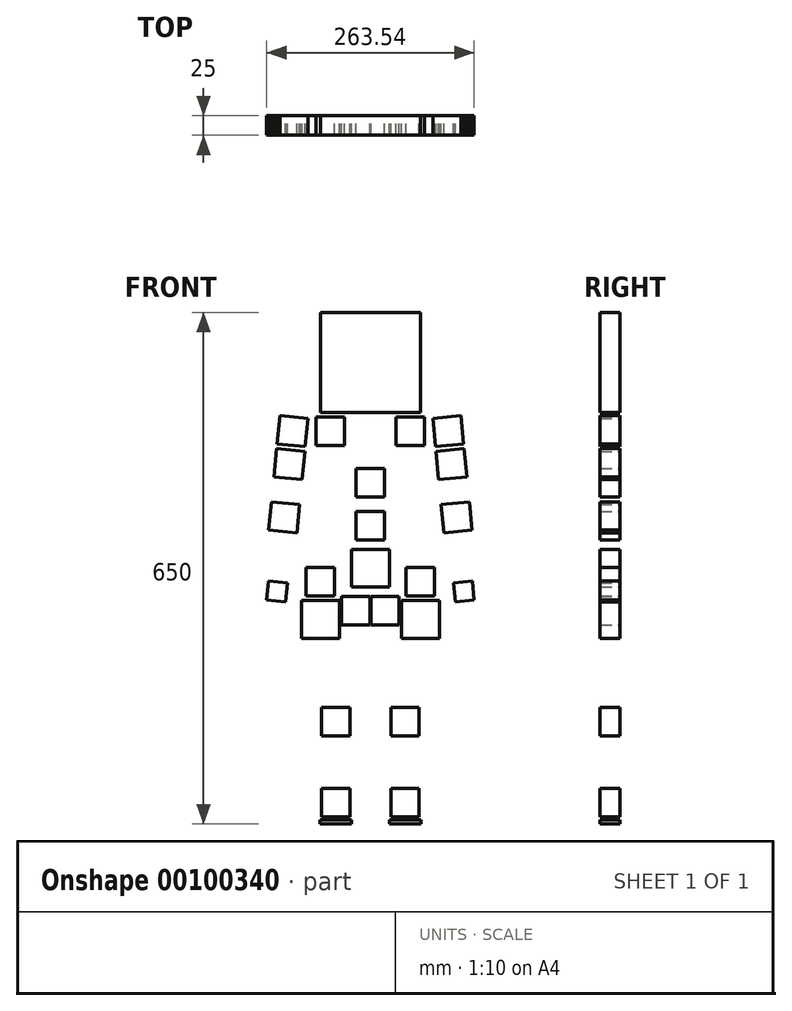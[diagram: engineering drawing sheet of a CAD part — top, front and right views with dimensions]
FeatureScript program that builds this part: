
annotation { "Feature Type Name" : "Feature", "Feature Type Description" : "" }
export const myFeature = defineFeature(function(context is Context, id is Id, definition is map)
    precondition{}
    {
        {
            var Q0;
            Q0=qCreatedBy(makeId("Front.planeOp"),FACE);
            var sketch = newSketch(context, id + "F0", { "sketchPlane" : qUnion([Q0])});
            skLineSegment(sketch, "E0.bottom", {"start": v(-190.27, 650) * mm, "end": v(190.27, 650) * mm, "construction": true});
            skLineSegment(sketch, "E0.top", {"start": v(-190.27, 0) * mm, "end": v(190.27, 0) * mm, "construction": true});
            skLineSegment(sketch, "E1", {"start": v(0, 0) * mm, "end": v(0, 650) * mm, "construction": true});
            skLineSegment(sketch, "E2", {"start": v(-190.27, 520) * mm, "end": v(190.27, 520) * mm, "construction": true});
            skLineSegment(sketch, "E3", {"start": v(-190.27, 650) * mm, "end": v(-190.27, 520) * mm, "construction": true});
            skLineSegment(sketch, "E4", {"start": v(-190.27, 0) * mm, "end": v(-190.27, 520) * mm, "construction": true});
            skLineSegment(sketch, "E5", {"start": v(-190.27, 260) * mm, "end": v(190.27, 260) * mm, "construction": true});
            skLineSegment(sketch, "E6", {"start": v(-81.25, 260) * mm, "end": v(-81.25, 0) * mm, "construction": true});
            skLineSegment(sketch, "E7", {"start": v(81.25, 260) * mm, "end": v(81.25, 0) * mm, "construction": true});
            skLineSegment(sketch, "E8", {"start": v(-81.25, 130) * mm, "end": v(81.25, 130) * mm, "construction": true});
            skLineSegment(sketch, "E9", {"start": v(190.27, 650) * mm, "end": v(190.27, 0) * mm, "construction": true});
            skLineSegment(sketch, "E10", {"start": v(190.27, 325) * mm, "end": v(-190.27, 325) * mm, "construction": true});
            skSolve(sketch);
        }
        {
            var Q0;
            Q0=qCreatedBy(makeId("Front.planeOp"),FACE);
            var sketch = newSketch(context, id + "F1", { "sketchPlane" : qUnion([Q0])});
            skLineSegment(sketch, "E11", {"start": v(0, 260) * mm, "end": v(63.5, 260) * mm, "construction": true});
            skLineSegment(sketch, "E12", {"start": v(63.5, 260) * mm, "end": v(44, 130) * mm, "construction": true});
            skLineSegment(sketch, "E13", {"start": v(44, 130) * mm, "end": v(44, 27.18) * mm, "construction": true});
            skLineSegment(sketch, "E14", {"start": v(44, 27.18) * mm, "end": v(44, 0) * mm, "construction": true});
            skLineSegment(sketch, "E15", {"start": v(0, 0) * mm, "end": v(0, 650) * mm, "construction": true});
            skLineSegment(sketch, "E16.bottom", {"start": v(62, 9.18) * mm, "end": v(26, 9.18) * mm});
            skLineSegment(sketch, "E16.top", {"start": v(62, 45.18) * mm, "end": v(26, 45.18) * mm});
            skLineSegment(sketch, "E16.left", {"start": v(62, 9.18) * mm, "end": v(62, 45.18) * mm});
            skLineSegment(sketch, "E16.right", {"start": v(26, 9.18) * mm, "end": v(26, 45.18) * mm});
            skPoint(sketch, "E16.middle", {"position": v(44, 27.18) * mm});
            skLineSegment(sketch, "E17.bottom", {"start": v(62, 112) * mm, "end": v(26, 112) * mm});
            skLineSegment(sketch, "E17.top", {"start": v(62, 148) * mm, "end": v(26, 148) * mm});
            skLineSegment(sketch, "E17.left", {"start": v(62, 112) * mm, "end": v(62, 148) * mm});
            skLineSegment(sketch, "E17.right", {"start": v(26, 112) * mm, "end": v(26, 148) * mm});
            skPoint(sketch, "E17.middle", {"position": v(44, 130) * mm});
            skLineSegment(sketch, "E18.bottom", {"start": v(87.5, 236) * mm, "end": v(39.5, 236) * mm});
            skLineSegment(sketch, "E18.top", {"start": v(87.5, 284) * mm, "end": v(39.5, 284) * mm});
            skLineSegment(sketch, "E18.left", {"start": v(87.5, 236) * mm, "end": v(87.5, 284) * mm});
            skLineSegment(sketch, "E18.right", {"start": v(39.5, 236) * mm, "end": v(39.5, 284) * mm});
            skPoint(sketch, "E18.middle", {"position": v(63.5, 260) * mm});
            skLineSegment(sketch, "E19.bottom", {"start": v(81.5, 290) * mm, "end": v(45.5, 290) * mm});
            skLineSegment(sketch, "E19.top", {"start": v(81.5, 326) * mm, "end": v(45.5, 326) * mm});
            skLineSegment(sketch, "E19.left", {"start": v(81.5, 290) * mm, "end": v(81.5, 326) * mm});
            skLineSegment(sketch, "E19.right", {"start": v(45.5, 290) * mm, "end": v(45.5, 326) * mm});
            skPoint(sketch, "E19.middle", {"position": v(63.5, 308) * mm});
            skLineSegment(sketch, "E20.bottom", {"start": v(36.5, 253) * mm, "end": v(0.5, 253) * mm});
            skLineSegment(sketch, "E20.top", {"start": v(36.5, 289) * mm, "end": v(0.5, 289) * mm});
            skLineSegment(sketch, "E20.left", {"start": v(36.5, 253) * mm, "end": v(36.5, 289) * mm});
            skLineSegment(sketch, "E20.right", {"start": v(0.5, 253) * mm, "end": v(0.5, 289) * mm});
            skPoint(sketch, "E20.middle", {"position": v(18.5, 271) * mm});
            skLineSegment(sketch, "E21.bottom", {"start": v(24, 301) * mm, "end": v(-24, 301) * mm});
            skLineSegment(sketch, "E21.top", {"start": v(24, 349) * mm, "end": v(-24, 349) * mm});
            skLineSegment(sketch, "E21.left", {"start": v(24, 301) * mm, "end": v(24, 349) * mm});
            skLineSegment(sketch, "E21.right", {"start": v(-24, 301) * mm, "end": v(-24, 349) * mm});
            skPoint(sketch, "E21.middle", {"position": v(0, 325) * mm});
            skLineSegment(sketch, "E22.bottom", {"start": v(18, 361) * mm, "end": v(-18, 361) * mm});
            skLineSegment(sketch, "E22.top", {"start": v(18, 397) * mm, "end": v(-18, 397) * mm});
            skLineSegment(sketch, "E22.left", {"start": v(18, 361) * mm, "end": v(18, 397) * mm});
            skLineSegment(sketch, "E22.right", {"start": v(-18, 361) * mm, "end": v(-18, 397) * mm});
            skPoint(sketch, "E22.middle", {"position": v(0, 379) * mm});
            skLineSegment(sketch, "E23.bottom", {"start": v(18, 415.45) * mm, "end": v(-18, 415.45) * mm});
            skLineSegment(sketch, "E23.top", {"start": v(18, 451.45) * mm, "end": v(-18, 451.45) * mm});
            skLineSegment(sketch, "E23.left", {"start": v(18, 415.45) * mm, "end": v(18, 451.45) * mm});
            skLineSegment(sketch, "E23.right", {"start": v(-18, 415.45) * mm, "end": v(-18, 451.45) * mm});
            skPoint(sketch, "E23.middle", {"position": v(0, 433.45) * mm});
            skLineSegment(sketch, "E24.MirrorCS", {"start": v(-26, 9.18) * mm, "end": v(-26, 45.18) * mm});
            skLineSegment(sketch, "E25.MirrorCS", {"start": v(-45.5, 290) * mm, "end": v(-45.5, 326) * mm});
            skLineSegment(sketch, "E26.MirrorCS", {"start": v(-81.5, 290) * mm, "end": v(-81.5, 326) * mm});
            skPoint(sketch, "E27.MirrorP", {"position": v(-44, 27.18) * mm});
            skLineSegment(sketch, "E28.MirrorCS", {"start": v(-87.5, 236) * mm, "end": v(-39.5, 236) * mm});
            skLineSegment(sketch, "E29.MirrorCS", {"start": v(-87.5, 284) * mm, "end": v(-39.5, 284) * mm});
            skLineSegment(sketch, "E30.MirrorCS", {"start": v(-81.5, 326) * mm, "end": v(-45.5, 326) * mm});
            skLineSegment(sketch, "E31.MirrorCS", {"start": v(-36.5, 289) * mm, "end": v(-0.5, 289) * mm});
            skLineSegment(sketch, "E32.MirrorCS", {"start": v(-62, 9.18) * mm, "end": v(-62, 45.18) * mm});
            skLineSegment(sketch, "E33.MirrorCS", {"start": v(-62, 45.18) * mm, "end": v(-26, 45.18) * mm});
            skLineSegment(sketch, "E34.MirrorCS", {"start": v(-62, 112) * mm, "end": v(-26, 112) * mm});
            skLineSegment(sketch, "E35.MirrorCS", {"start": v(-87.5, 236) * mm, "end": v(-87.5, 284) * mm});
            skLineSegment(sketch, "E36.MirrorCS", {"start": v(-62, 148) * mm, "end": v(-26, 148) * mm});
            skLineSegment(sketch, "E37.MirrorCS", {"start": v(0, 260) * mm, "end": v(-63.5, 260) * mm, "construction": true});
            skLineSegment(sketch, "E38.MirrorCS", {"start": v(-62, 112) * mm, "end": v(-62, 148) * mm});
            skLineSegment(sketch, "E39.MirrorCS", {"start": v(-62, 9.18) * mm, "end": v(-26, 9.18) * mm});
            skLineSegment(sketch, "E40.MirrorCS", {"start": v(-44, 27.18) * mm, "end": v(-44, 0) * mm, "construction": true});
            skPoint(sketch, "E41.MirrorP", {"position": v(-63.5, 308) * mm});
            skLineSegment(sketch, "E42.MirrorCS", {"start": v(-81.5, 290) * mm, "end": v(-45.5, 290) * mm});
            skLineSegment(sketch, "E43.MirrorCS", {"start": v(-63.5, 260) * mm, "end": v(-44, 130) * mm, "construction": true});
            skLineSegment(sketch, "E44.MirrorCS", {"start": v(-44, 130) * mm, "end": v(-44, 27.18) * mm, "construction": true});
            skPoint(sketch, "E45.MirrorP", {"position": v(-63.5, 260) * mm});
            skPoint(sketch, "E46.MirrorP", {"position": v(-18.5, 271) * mm});
            skLineSegment(sketch, "E47.MirrorCS", {"start": v(-36.5, 253) * mm, "end": v(-36.5, 289) * mm});
            skLineSegment(sketch, "E48.MirrorCS", {"start": v(-26, 112) * mm, "end": v(-26, 148) * mm});
            skLineSegment(sketch, "E49.MirrorCS", {"start": v(-0.5, 253) * mm, "end": v(-0.5, 289) * mm});
            skPoint(sketch, "E50.MirrorP", {"position": v(-44, 130) * mm});
            skLineSegment(sketch, "E51.MirrorCS", {"start": v(-39.5, 236) * mm, "end": v(-39.5, 284) * mm});
            skLineSegment(sketch, "E52.MirrorCS", {"start": v(-36.5, 253) * mm, "end": v(-0.5, 253) * mm});
            skLineSegment(sketch, "E53", {"start": v(0, 499) * mm, "end": v(98.88, 499) * mm, "construction": true});
            skPoint(sketch, "E54.middle", {"position": v(98.88, 499) * mm});
            skLineSegment(sketch, "E55.bottom", {"start": v(68.88, 481) * mm, "end": v(32.88, 481) * mm});
            skLineSegment(sketch, "E55.top", {"start": v(68.88, 517) * mm, "end": v(32.88, 517) * mm});
            skLineSegment(sketch, "E55.left", {"start": v(68.88, 481) * mm, "end": v(68.88, 517) * mm});
            skLineSegment(sketch, "E55.right", {"start": v(32.88, 481) * mm, "end": v(32.88, 517) * mm});
            skPoint(sketch, "E55.middle", {"position": v(50.88, 499) * mm});
            skLineSegment(sketch, "E56", {"start": v(98.88, 499) * mm, "end": v(109.51, 389.55) * mm, "construction": true});
            skLineSegment(sketch, "E57", {"start": v(109.51, 389.55) * mm, "end": v(118.66, 295.4) * mm, "construction": true});
            skLineSegment(sketch, "E58", {"start": v(118.66, 295.4) * mm, "end": v(124.13, 239.15) * mm, "construction": true});
            skLineSegment(sketch, "E59.bottom", {"start": v(129.17, 373.38) * mm, "end": v(93.34, 369.9) * mm});
            skLineSegment(sketch, "E59.top", {"start": v(125.69, 409.2) * mm, "end": v(89.86, 405.73) * mm});
            skLineSegment(sketch, "E59.left", {"start": v(129.17, 373.38) * mm, "end": v(125.69, 409.2) * mm});
            skLineSegment(sketch, "E59.right", {"start": v(93.34, 369.9) * mm, "end": v(89.86, 405.73) * mm});
            skPoint(sketch, "E59.middle", {"position": v(109.51, 389.55) * mm});
            skLineSegment(sketch, "E60.bottom", {"start": v(122.6, 441.02) * mm, "end": v(86.77, 437.54) * mm});
            skLineSegment(sketch, "E60.top", {"start": v(119.12, 476.85) * mm, "end": v(83.29, 473.37) * mm});
            skLineSegment(sketch, "E60.left", {"start": v(122.6, 441.02) * mm, "end": v(119.12, 476.85) * mm});
            skLineSegment(sketch, "E60.right", {"start": v(86.77, 437.54) * mm, "end": v(83.29, 473.37) * mm});
            skPoint(sketch, "E60.middle", {"position": v(102.94, 457.2) * mm});
            skLineSegment(sketch, "E61.bottom", {"start": v(118.54, 482.83) * mm, "end": v(82.7, 479.34) * mm});
            skLineSegment(sketch, "E61.top", {"start": v(115.05, 518.66) * mm, "end": v(79.22, 515.17) * mm});
            skLineSegment(sketch, "E61.left", {"start": v(118.54, 482.83) * mm, "end": v(115.05, 518.66) * mm});
            skLineSegment(sketch, "E61.right", {"start": v(82.7, 479.34) * mm, "end": v(79.22, 515.17) * mm});
            skLineSegment(sketch, "E62.bottom", {"start": v(107.88, 282.3) * mm, "end": v(105.56, 306.19) * mm});
            skLineSegment(sketch, "E62.top", {"start": v(131.77, 284.62) * mm, "end": v(129.45, 308.51) * mm});
            skLineSegment(sketch, "E62.left", {"start": v(107.88, 282.3) * mm, "end": v(131.77, 284.62) * mm});
            skLineSegment(sketch, "E62.right", {"start": v(105.56, 306.19) * mm, "end": v(129.45, 308.51) * mm});
            skPoint(sketch, "E62.middle", {"position": v(118.66, 295.4) * mm});
            skPoint(sketch, "E63.MirrorP", {"position": v(-98.88, 499) * mm});
            skPoint(sketch, "E64.MirrorP", {"position": v(-102.94, 457.2) * mm});
            skPoint(sketch, "E65.MirrorP", {"position": v(-109.51, 389.55) * mm});
            skLineSegment(sketch, "E66.MirrorCS", {"start": v(-122.6, 441.02) * mm, "end": v(-119.12, 476.85) * mm});
            skLineSegment(sketch, "E67.MirrorCS", {"start": v(-105.56, 306.19) * mm, "end": v(-129.45, 308.51) * mm});
            skLineSegment(sketch, "E68.MirrorCS", {"start": v(-118.54, 482.83) * mm, "end": v(-82.7, 479.34) * mm});
            skLineSegment(sketch, "E69.MirrorCS", {"start": v(0, 499) * mm, "end": v(-98.88, 499) * mm, "construction": true});
            skLineSegment(sketch, "E70.MirrorCS", {"start": v(-118.66, 295.4) * mm, "end": v(-124.13, 239.15) * mm, "construction": true});
            skLineSegment(sketch, "E71.MirrorCS", {"start": v(-82.7, 479.34) * mm, "end": v(-79.22, 515.17) * mm});
            skLineSegment(sketch, "E72.MirrorCS", {"start": v(-86.77, 437.54) * mm, "end": v(-83.29, 473.37) * mm});
            skLineSegment(sketch, "E73.MirrorCS", {"start": v(-115.05, 518.66) * mm, "end": v(-79.22, 515.17) * mm});
            skLineSegment(sketch, "E74.MirrorCS", {"start": v(-32.88, 481) * mm, "end": v(-32.88, 517) * mm});
            skLineSegment(sketch, "E75.MirrorCS", {"start": v(-68.88, 481) * mm, "end": v(-32.88, 481) * mm});
            skLineSegment(sketch, "E76.MirrorCS", {"start": v(-129.17, 373.38) * mm, "end": v(-93.34, 369.9) * mm});
            skPoint(sketch, "E77.MirrorP", {"position": v(-118.66, 295.4) * mm});
            skLineSegment(sketch, "E78.MirrorCS", {"start": v(-125.69, 409.2) * mm, "end": v(-89.86, 405.73) * mm});
            skLineSegment(sketch, "E79.MirrorCS", {"start": v(-68.88, 517) * mm, "end": v(-32.88, 517) * mm});
            skLineSegment(sketch, "E80.MirrorCS", {"start": v(-118.54, 482.83) * mm, "end": v(-115.05, 518.66) * mm});
            skPoint(sketch, "E81.MirrorP", {"position": v(-50.88, 499) * mm});
            skLineSegment(sketch, "E82.MirrorCS", {"start": v(-107.88, 282.3) * mm, "end": v(-105.56, 306.19) * mm});
            skLineSegment(sketch, "E83.MirrorCS", {"start": v(-107.88, 282.3) * mm, "end": v(-131.77, 284.62) * mm});
            skLineSegment(sketch, "E84.MirrorCS", {"start": v(-119.12, 476.85) * mm, "end": v(-83.29, 473.37) * mm});
            skLineSegment(sketch, "E85.MirrorCS", {"start": v(-98.88, 499) * mm, "end": v(-109.51, 389.55) * mm, "construction": true});
            skLineSegment(sketch, "E86.MirrorCS", {"start": v(-109.51, 389.55) * mm, "end": v(-118.66, 295.4) * mm, "construction": true});
            skLineSegment(sketch, "E87.MirrorCS", {"start": v(-93.34, 369.9) * mm, "end": v(-89.86, 405.73) * mm});
            skLineSegment(sketch, "E88.MirrorCS", {"start": v(-68.88, 481) * mm, "end": v(-68.88, 517) * mm});
            skLineSegment(sketch, "E89.MirrorCS", {"start": v(-129.17, 373.38) * mm, "end": v(-125.69, 409.2) * mm});
            skLineSegment(sketch, "E90.MirrorCS", {"start": v(-122.6, 441.02) * mm, "end": v(-86.77, 437.54) * mm});
            skLineSegment(sketch, "E91.MirrorCS", {"start": v(-131.77, 284.62) * mm, "end": v(-129.45, 308.51) * mm});
            skLineSegment(sketch, "E92.bottom", {"start": v(63.5, 650) * mm, "end": v(-63.5, 650) * mm});
            skLineSegment(sketch, "E92.top", {"start": v(63.5, 523) * mm, "end": v(-63.5, 523) * mm});
            skLineSegment(sketch, "E92.left", {"start": v(63.5, 650) * mm, "end": v(63.5, 523) * mm});
            skLineSegment(sketch, "E92.right", {"start": v(-63.5, 650) * mm, "end": v(-63.5, 523) * mm});
            skPoint(sketch, "E92.middle", {"position": v(0, 586.5) * mm});
            skCircle(sketch, "E93", {"center": v(18.5, 271) * mm, "radius": 25.46 * mm, "construction": true});
            skCircle(sketch, "E94", {"center": v(0, 325) * mm, "radius": 33.94 * mm, "construction": true});
            skLineSegment(sketch, "E95.bottom", {"start": v(24, 5) * mm, "end": v(64, 5) * mm});
            skLineSegment(sketch, "E95.top", {"start": v(24, 0) * mm, "end": v(64, 0) * mm});
            skLineSegment(sketch, "E95.left", {"start": v(24, 5) * mm, "end": v(24, 0) * mm});
            skLineSegment(sketch, "E95.right", {"start": v(64, 5) * mm, "end": v(64, 0) * mm});
            skLineSegment(sketch, "E96.MirrorCS", {"start": v(-24, 5) * mm, "end": v(-64, 5) * mm});
            skLineSegment(sketch, "E97.MirrorCS", {"start": v(-64, 5) * mm, "end": v(-64, 0) * mm});
            skLineSegment(sketch, "E98.MirrorCS", {"start": v(-24, 5) * mm, "end": v(-24, 0) * mm});
            skLineSegment(sketch, "E99.MirrorCS", {"start": v(-24, 0) * mm, "end": v(-64, 0) * mm});
            skCircle(sketch, "E100", {"center": v(44, 27.18) * mm, "radius": 25.46 * mm, "construction": true});
            skCircle(sketch, "E101", {"center": v(98.88, 499) * mm, "radius": 261.07 * mm, "construction": true});
            skCircle(sketch, "E102", {"center": v(98.88, 499) * mm, "radius": 109.96 * mm, "construction": true});
            skCircle(sketch, "E103", {"center": v(98.88, 499) * mm, "radius": 204.55 * mm, "construction": true});
            skSolve(sketch);
        }
        {
            var Q0;
            Q0=qSketchRegion(id+"F1",true);
            extrude(context, id + "F2", {"entities" : qUnion([Q0]), "depth" : 25 * mm});
        }
    });
